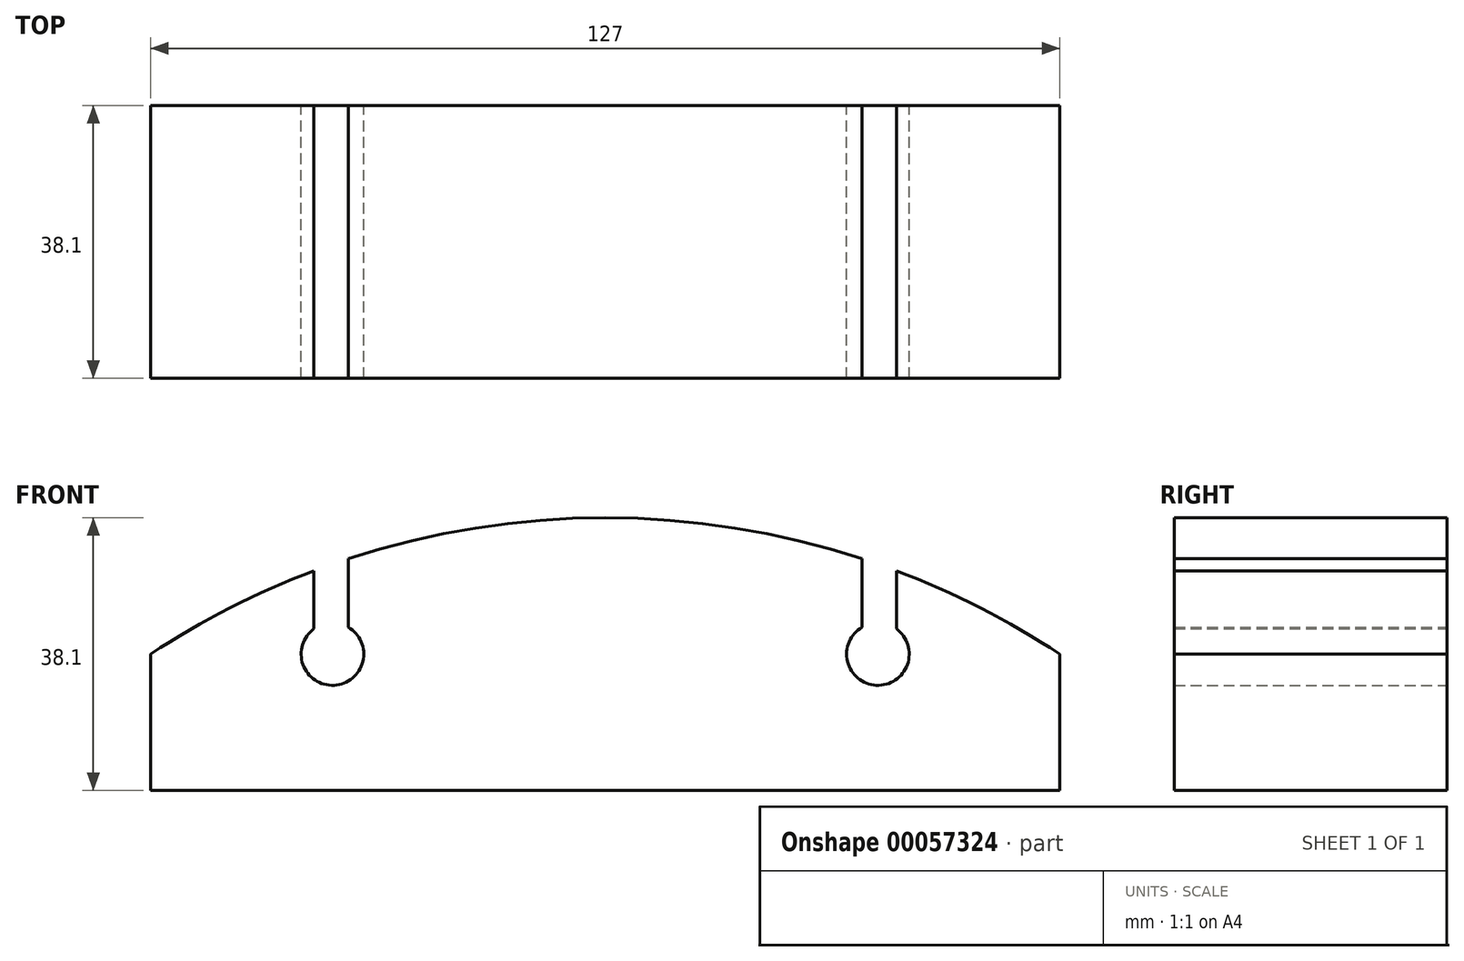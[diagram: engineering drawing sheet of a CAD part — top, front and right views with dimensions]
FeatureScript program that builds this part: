
annotation { "Feature Type Name" : "Feature", "Feature Type Description" : "" }
export const myFeature = defineFeature(function(context is Context, id is Id, definition is map)
    precondition{}
    {
        {
            var Q0;
            Q0=qCreatedBy(makeId("Front.planeOp"),FACE);
            var sketch = newSketch(context, id + "F0", { "sketchPlane" : qUnion([Q0])});
            skLineSegment(sketch, "E0.rect.top", {"start": v(63.5, -9.53) * mm, "end": v(-63.5, -9.53) * mm});
            skLineSegment(sketch, "E0.rect.left", {"start": v(63.5, 9.52) * mm, "end": v(63.5, -9.53) * mm});
            skLineSegment(sketch, "E0.rect.right", {"start": v(-63.5, 9.52) * mm, "end": v(-63.5, -9.52) * mm});
            skPoint(sketch, "E0.rect.middle", {"position": v(0, 0) * mm});
            skArc(sketch, "E1", {"start": v(63.5, 9.52) * mm, "mid": v(52.41, 15.98) * mm, "end": v(40.68, 21.17) * mm});
            skLineSegment(sketch, "E2", {"start": v(-40.68, 21.17) * mm, "end": v(-40.68, 13.05) * mm});
            skLineSegment(sketch, "E3", {"start": v(-35.9, 22.85) * mm, "end": v(-35.9, 13.3) * mm});
            skArc(sketch, "E4.trimOffspring", {"start": v(-40.68, 21.17) * mm, "mid": v(-52.41, 15.98) * mm, "end": v(-63.5, 9.52) * mm});
            skArc(sketch, "E5", {"start": v(-40.68, 13.05) * mm, "mid": v(-37.88, 5.16) * mm, "end": v(-35.9, 13.3) * mm});
            skLineSegment(sketch, "E6.MirrorCS", {"start": v(35.9, 22.85) * mm, "end": v(35.9, 13.3) * mm});
            skLineSegment(sketch, "E7.MirrorCS", {"start": v(40.68, 21.17) * mm, "end": v(40.68, 13.05) * mm});
            skArc(sketch, "E8.MirrorCS", {"start": v(40.68, 13.05) * mm, "mid": v(37.88, 5.16) * mm, "end": v(35.9, 13.3) * mm});
            skArc(sketch, "E9.trimOffspring", {"start": v(35.9, 22.85) * mm, "mid": v(0, 28.57) * mm, "end": v(-35.9, 22.85) * mm});
            skSolve(sketch);
        }
        {
            var Q0;
            Q0=makeQuery(id+"F0.imprint","IMPRINT",FACE,{"disambiguationData":[TD([[makeQuery(id+"F0.imprint","IMPRINT",EDGE,{"derivedFrom":sQuery(id+"F0.wireOp",EDGE,"E0.rect.top")}),-1.0]])]});
            extrude(context, id + "F1", {"entities" : qUnion([Q0]), "endBound" : BoundingType.SYMMETRIC, "depth" : 38.1 * mm});
        }
    });
